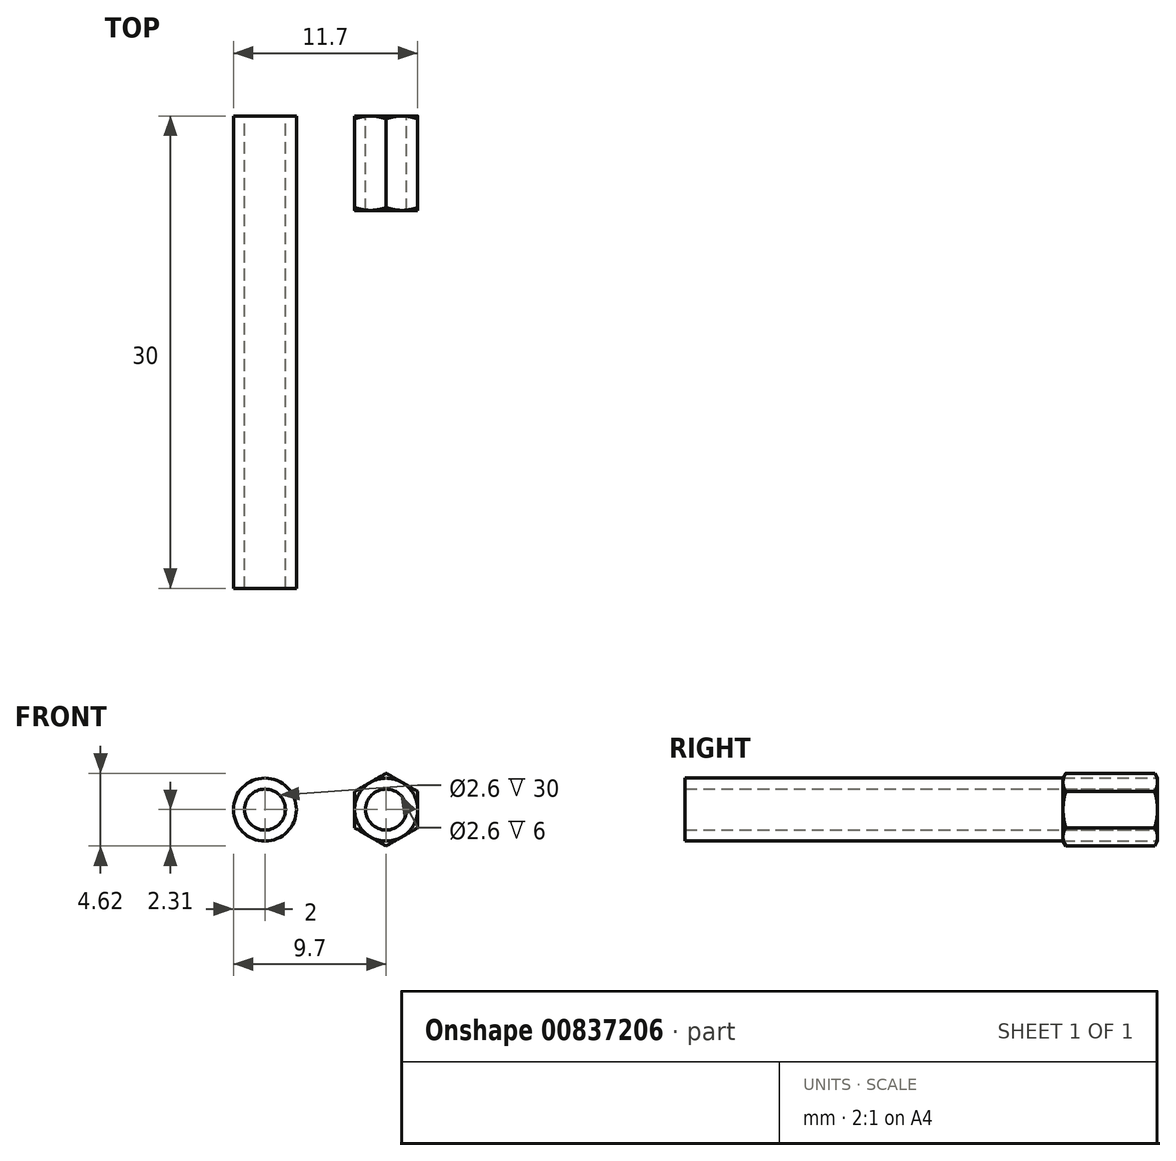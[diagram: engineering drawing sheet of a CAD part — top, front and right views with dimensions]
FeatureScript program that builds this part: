
annotation { "Feature Type Name" : "Feature", "Feature Type Description" : "" }
export const myFeature = defineFeature(function(context is Context, id is Id, definition is map)
    precondition{}
    {
        {
            var Q0;
            Q0=qCreatedBy(makeId("Front.planeOp"),FACE);
            var sketch = newSketch(context, id + "F0", { "sketchPlane" : qUnion([Q0])});
            skCircle(sketch, "E0.cCircle", {"center": v(0, 0) * mm, "radius": 2 * mm, "construction": true});
            skLineSegment(sketch, "E0.0", {"start": v(2, 1.15) * mm, "end": v(2, -1.15) * mm});
            skLineSegment(sketch, "E0.1", {"start": v(2, -1.15) * mm, "end": v(0, -2.3) * mm});
            skLineSegment(sketch, "E0.2", {"start": v(0, -2.3) * mm, "end": v(-2, -1.15) * mm});
            skLineSegment(sketch, "E0.3", {"start": v(-2, -1.15) * mm, "end": v(-2, 1.15) * mm});
            skLineSegment(sketch, "E0.4", {"start": v(-2, 1.15) * mm, "end": v(0, 2.3) * mm});
            skLineSegment(sketch, "E0.5", {"start": v(0, 2.3) * mm, "end": v(2, 1.15) * mm});
            skPoint(sketch, "E0.0.midPoint", {"position": v(2, 0) * mm});
            skCircle(sketch, "E1", {"center": v(0, 0) * mm, "radius": 1.3 * mm});
            skSolve(sketch);
        }
        {
            var Q0;
            Q0=makeQuery(id+"F0.imprint","IMPRINT",FACE,{"disambiguationData":[TD([[makeQuery(id+"F0.imprint","IMPRINT",EDGE,{"derivedFrom":sQuery(id+"F0.wireOp",EDGE,"E0.0")}),-1.0]])]});
            extrude(context, id + "F1", {"entities" : qUnion([Q0]), "depth" : 6 * mm});
        }
        {
            var Q0;
            Q0=qCreatedBy(makeId("Top.planeOp"),FACE);
            var sketch = newSketch(context, id + "F2", { "sketchPlane" : qUnion([Q0])});
            skLineSegment(sketch, "E2", {"start": v(2, -6) * mm, "end": v(7.2, -6) * mm});
            skLineSegment(sketch, "E3", {"start": v(7.2, -6) * mm, "end": v(7.2, -3) * mm});
            skLineSegment(sketch, "E4", {"start": v(7.2, -3) * mm, "end": v(2, -6) * mm});
            skLineSegment(sketch, "E5", {"start": v(0, -7.82) * mm, "end": v(0, 7.75) * mm});
            skLineSegment(sketch, "E6", {"start": v(0, -3) * mm, "end": v(-4.13, -3) * mm});
            skLineSegment(sketch, "E7", {"start": v(-4.13, -3) * mm, "end": v(6.87, -3) * mm});
            skLineSegment(sketch, "E8.MirrorCS", {"start": v(7.2, -3) * mm, "end": v(2, 0) * mm});
            skLineSegment(sketch, "E9.MirrorCS", {"start": v(2, 0) * mm, "end": v(7.2, 0) * mm});
            skLineSegment(sketch, "E10.MirrorCS", {"start": v(7.2, 0) * mm, "end": v(7.2, -3) * mm});
            skSolve(sketch);
        }
        {
            var Q0;
            Q0=makeQuery(id+"F2.imprint","IMPRINT",FACE,{"disambiguationData":[TD([[makeQuery(id+"F2.imprint","IMPRINT",EDGE,{"derivedFrom":sQuery(id+"F2.wireOp",EDGE,"E8.MirrorCS")}),-1.0]])]});
            var Q1;
            Q1=makeQuery(id+"F2.imprint","IMPRINT",FACE,{"disambiguationData":[TD([[makeQuery(id+"F2.imprint","IMPRINT",EDGE,{"derivedFrom":sQuery(id+"F2.wireOp",EDGE,"E2")}),1.0]])]});
            var Q2;
            Q2=sQuery(id+"F2.wireOp",EDGE,"E5");
            revolve(context, id + "F3", {"operationType" : NewBodyOperationType.REMOVE, "entities" : qUnion([Q0, Q1]), "axis" : qUnion([Q2]), "revolveType" : RevolveType.FULL});
        }
        {
            var Q0;
            Q0=qCreatedBy(makeId("Front.planeOp"),FACE);
            var sketch = newSketch(context, id + "F4", { "sketchPlane" : qUnion([Q0])});
            skCircle(sketch, "E11", {"center": v(0, 0) * mm, "radius": 2 * mm});
            skCircle(sketch, "E12", {"center": v(0, 0) * mm, "radius": 1.3 * mm});
            skSolve(sketch);
        }
        {
            var Q0;
            Q0=makeQuery(id+"F4.imprint","IMPRINT",FACE,{"disambiguationData":[TD([[makeQuery(id+"F4.imprint","IMPRINT",EDGE,{"derivedFrom":sQuery(id+"F4.wireOp",EDGE,"E11")}),1.0]])]});
            extrude(context, id + "F5", {"entities" : qUnion([Q0]), "depth" : 30 * mm});
        }
        {
            var Q0;
            Q0=makeQuery(id+"F5.opExtrude","SWEPT_BODY",BODY,{"disambiguationData":[OSD([sQuery(id+"F4.wireOp",EDGE,"E11"),sQuery(id+"F4.wireOp",EDGE,"E12")])]});
            transform(context, id + "F6", {"entities" : qUnion([Q0]), "transformType" : TransformType.TRANSLATION_3D, "dx" : -7.7 * mm, "dy" : 0 * mm, "dz" : 0 * mm, "makeCopy" : false});
        }
    });
